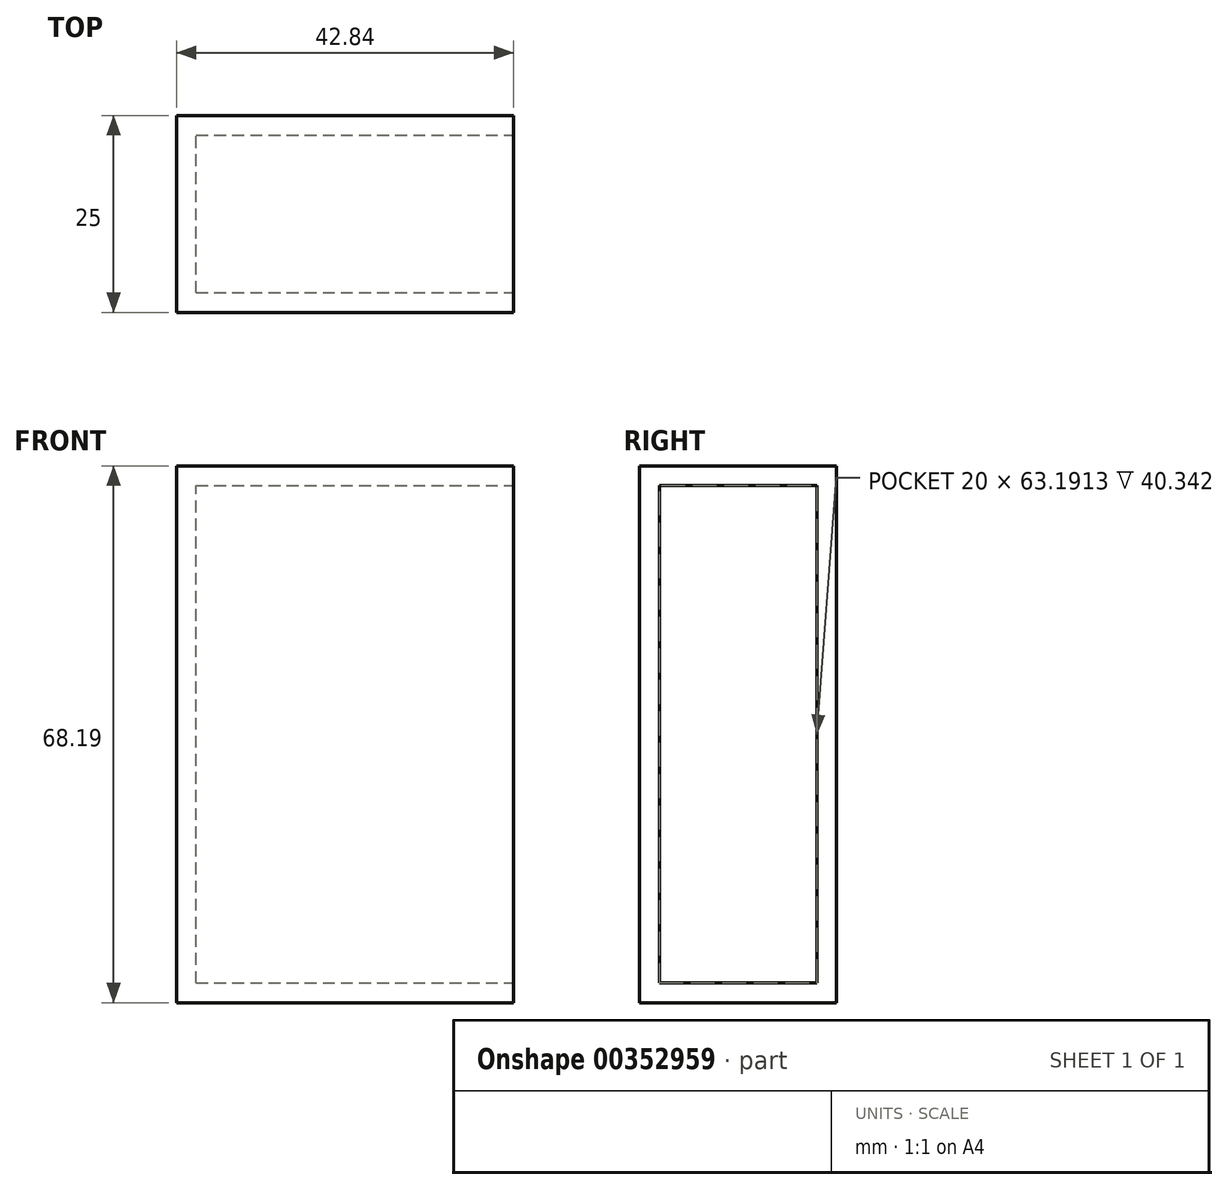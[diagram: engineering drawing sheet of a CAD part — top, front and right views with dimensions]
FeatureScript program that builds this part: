
annotation { "Feature Type Name" : "Feature", "Feature Type Description" : "" }
export const myFeature = defineFeature(function(context is Context, id is Id, definition is map)
    precondition{}
    {
        {
            var Q0;
            Q0=qCreatedBy(makeId("Front.planeOp"),FACE);
            var sketch = newSketch(context, id + "F0", { "sketchPlane" : qUnion([Q0])});
            skLineSegment(sketch, "E0.bottom", {"start": v(-82.11, 12) * mm, "end": v(-39.27, 12) * mm});
            skLineSegment(sketch, "E0.top", {"start": v(-82.11, 80.19) * mm, "end": v(-39.27, 80.19) * mm});
            skLineSegment(sketch, "E0.left", {"start": v(-82.11, 12) * mm, "end": v(-82.11, 80.19) * mm});
            skLineSegment(sketch, "E0.right", {"start": v(-39.27, 12) * mm, "end": v(-39.27, 80.19) * mm});
            skPoint(sketch, "E0.middle", {"position": v(-60.7, 46.1) * mm});
            skSolve(sketch);
        }
        {
            var Q0;
            Q0=makeQuery(id+"F0.imprint","IMPRINT",FACE,{"disambiguationData":[TD([[makeQuery(id+"F0.imprint","IMPRINT",EDGE,{"derivedFrom":sQuery(id+"F0.wireOp",EDGE,"E0.bottom")}),1.0]])]});
            extrude(context, id + "F1", {"entities" : qUnion([Q0]), "depth" : 25 * mm});
        }
        {
            var Q0;
            Q0=makeQuery(id+"F1.opExtrude","SWEPT_FACE",FACE,{"disambiguationData":[OSD([sQuery(id+"F0.wireOp",EDGE,"E0.right")])]});
            shell(context, id + "F2", {"entities" : qUnion([Q0]), "thickness" : 2.5 * mm});
        }
    });
